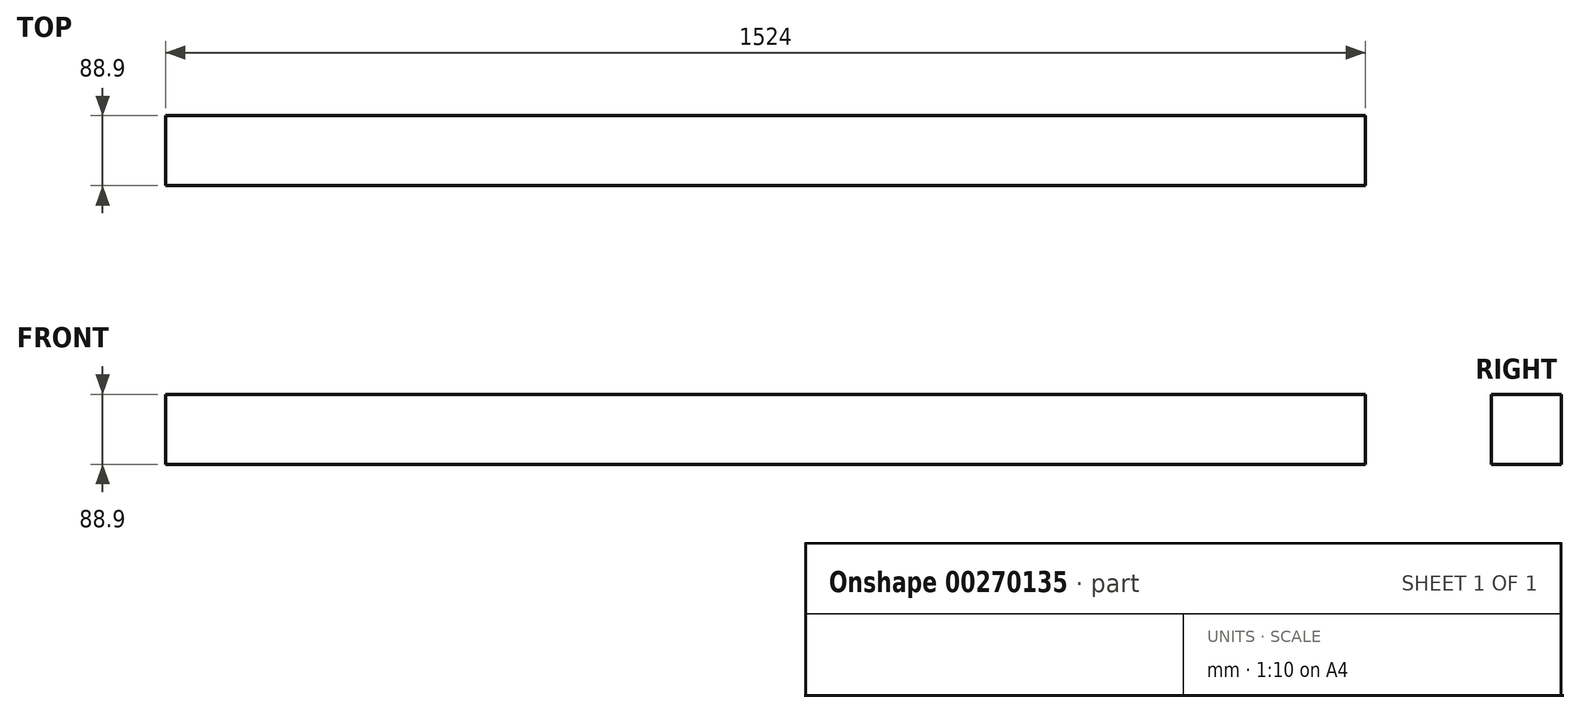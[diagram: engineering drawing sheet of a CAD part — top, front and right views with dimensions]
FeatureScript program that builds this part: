
annotation { "Feature Type Name" : "Feature", "Feature Type Description" : "" }
export const myFeature = defineFeature(function(context is Context, id is Id, definition is map)
    precondition{}
    {
        {
            var Q0;
            Q0=qCreatedBy(makeId("Right.planeOp"),FACE);
            var sketch = newSketch(context, id + "F0", { "sketchPlane" : qUnion([Q0])});
            skLineSegment(sketch, "E0.bottom", {"start": v(44.45, -44.45) * mm, "end": v(-44.45, -44.45) * mm});
            skLineSegment(sketch, "E0.top", {"start": v(44.45, 44.45) * mm, "end": v(-44.45, 44.45) * mm});
            skLineSegment(sketch, "E0.left", {"start": v(44.45, -44.45) * mm, "end": v(44.45, 44.45) * mm});
            skLineSegment(sketch, "E0.right", {"start": v(-44.45, -44.45) * mm, "end": v(-44.45, 44.45) * mm});
            skPoint(sketch, "E0.middle", {"position": v(0, 0) * mm});
            skSolve(sketch);
        }
        {
            var Q0;
            Q0=makeQuery(id+"F0.imprint","IMPRINT",FACE,{"disambiguationData":[TD([[makeQuery(id+"F0.imprint","IMPRINT",EDGE,{"derivedFrom":sQuery(id+"F0.wireOp",EDGE,"E0.bottom")}),-1.0]])]});
            extrude(context, id + "F1", {"entities" : qUnion([Q0]), "depth" : 1524 * mm});
        }
    });
